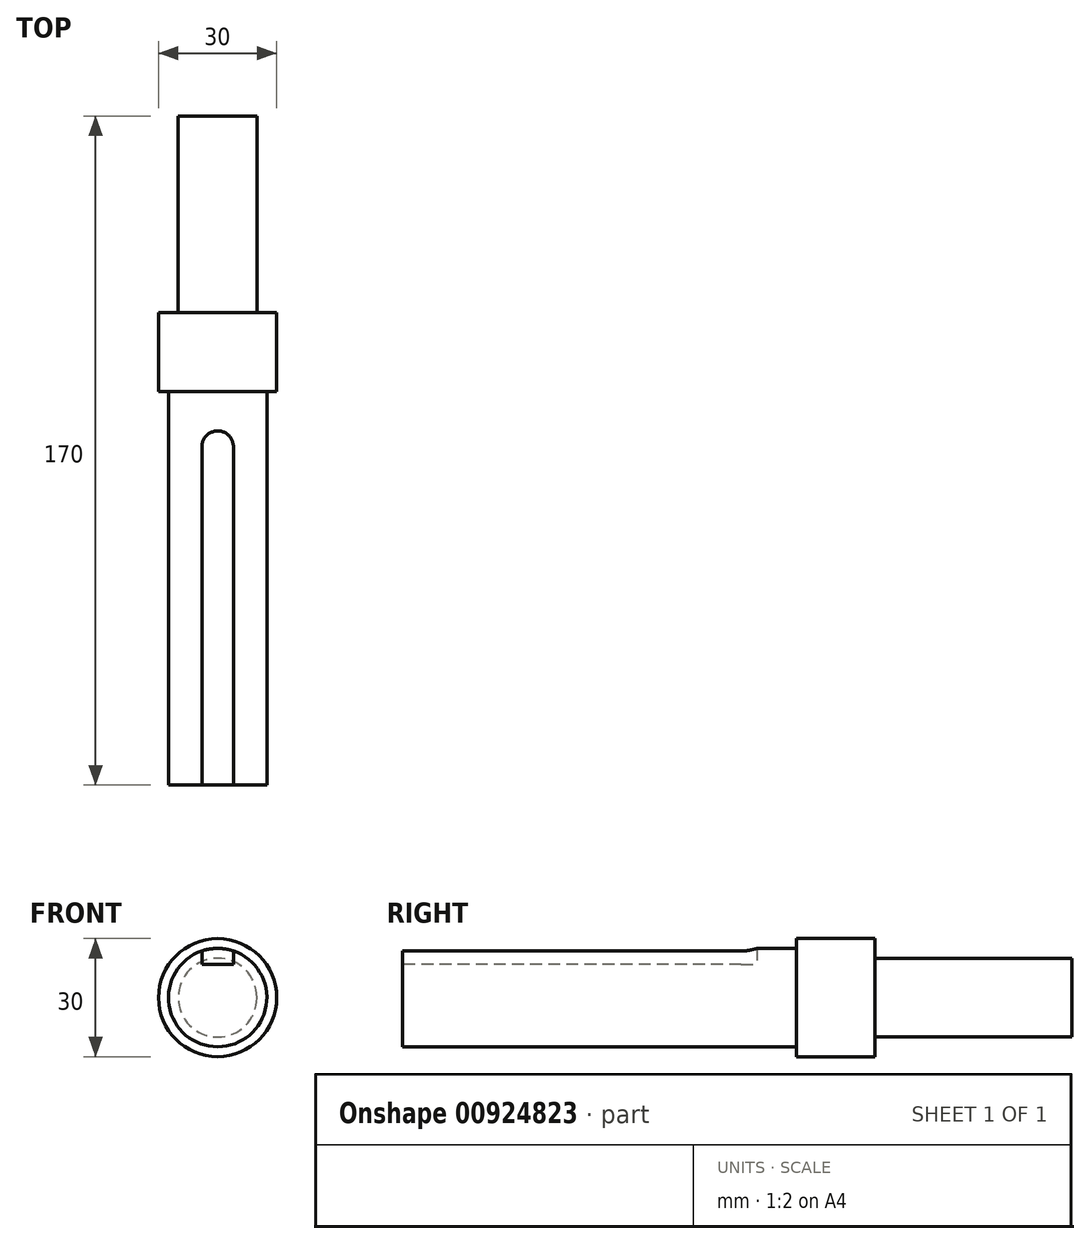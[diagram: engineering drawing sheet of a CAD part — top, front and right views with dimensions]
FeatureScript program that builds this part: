
annotation { "Feature Type Name" : "Feature", "Feature Type Description" : "" }
export const myFeature = defineFeature(function(context is Context, id is Id, definition is map)
    precondition{}
    {
        {
            var Q0;
            Q0=qCreatedBy(makeId("Right.planeOp"),FACE);
            var sketch = newSketch(context, id + "F0", { "sketchPlane" : qUnion([Q0])});
            skLineSegment(sketch, "E0", {"start": v(-110, 0) * mm, "end": v(-110, 12.5) * mm});
            skLineSegment(sketch, "E1", {"start": v(-110, 12.5) * mm, "end": v(-10, 12.5) * mm});
            skLineSegment(sketch, "E2", {"start": v(-10, 12.5) * mm, "end": v(-10, 15) * mm});
            skLineSegment(sketch, "E3", {"start": v(-10, 15) * mm, "end": v(10, 15) * mm});
            skLineSegment(sketch, "E4", {"start": v(10, 15) * mm, "end": v(10, 10) * mm});
            skLineSegment(sketch, "E5", {"start": v(10, 10) * mm, "end": v(60, 10) * mm});
            skLineSegment(sketch, "E6", {"start": v(60, 10) * mm, "end": v(60, 0) * mm});
            skLineSegment(sketch, "E7", {"start": v(60, 0) * mm, "end": v(-110, 0) * mm});
            skSolve(sketch);
        }
        {
            var Q0;
            Q0 = qSketchRegion(id + "F0", true);
            var Q1;
            Q1 = qConstructionFilter(qBodyType(qCreatedBy(id + "F0" ,EDGE), BodyType.WIRE), ConstructionObject.NO);
            var Q2;
            Q2=sQuery(id+"F0.wireOp",EDGE,"E7");
            revolve(context, id + "F1", {"surfaceOperationType" : NewSurfaceOperationType.NEW, "entities" : qUnion([Q0]), "surfaceEntities" : qUnion([Q1]), "axis" : qUnion([Q2]), "revolveType" : RevolveType.FULL});
        }
        {
            var Q0;
            Q0=makeQuery(id+"F1.opRevolve","SWEPT_FACE",FACE,{"disambiguationData":[OSD([sQuery(id+"F0.wireOp",EDGE,"E0")])]});
            var sketch = newSketch(context, id + "F2", { "sketchPlane" : qUnion([Q0])});
            skLineSegment(sketch, "E8.bottom", {"start": v(-4, 12.5) * mm, "end": v(4, 12.5) * mm});
            skLineSegment(sketch, "E8.top", {"start": v(-4, 8.5) * mm, "end": v(4, 8.5) * mm});
            skLineSegment(sketch, "E8.left", {"start": v(-4, 12.5) * mm, "end": v(-4, 8.5) * mm});
            skLineSegment(sketch, "E8.right", {"start": v(4, 12.5) * mm, "end": v(4, 8.5) * mm});
            skSolve(sketch);
        }
        {
            var Q0;
            Q0 = qSketchRegion(id + "F2", true);
            var Q1;
            Q1=makeQuery(id+"F1.opRevolve","SWEPT_FACE",FACE,{"disambiguationData":[OSD([sQuery(id+"F0.wireOp",EDGE,"E2")])]});
            extrude(context, id + "F3", {"entities" : qUnion([Q0]), "operationType" : NewBodyOperationType.REMOVE, "oppositeDirection" : true, "depth" : 90 * mm, "endBoundEntityFace" : qUnion([Q1]), "offsetDistance" : 25 * mm});
        }
        {
            var Q0;
            Q0=makeQuery(id+"F3.boolean.opBoolean","COPY",EDGE,{"derivedFrom":makeQuery(id+"F3.opExtrude","CAP_EDGE",EDGE,{"disambiguationData":[OSD([sQuery(id+"F2.wireOp",EDGE,"E8.left")])],"isStart":false})});
            var Q1;
            Q1=makeQuery(id+"F3.boolean.opBoolean","COPY",EDGE,{"derivedFrom":makeQuery(id+"F3.opExtrude","CAP_EDGE",EDGE,{"disambiguationData":[OSD([sQuery(id+"F2.wireOp",EDGE,"E8.right")])],"isStart":false})});
            fillet(context, id + "F4", {"entities" : qUnion([Q0, Q1]), "radius" : 4 * mm, "tangentPropagation" : true, "allowEdgeOverflow" : false});
        }
    });
